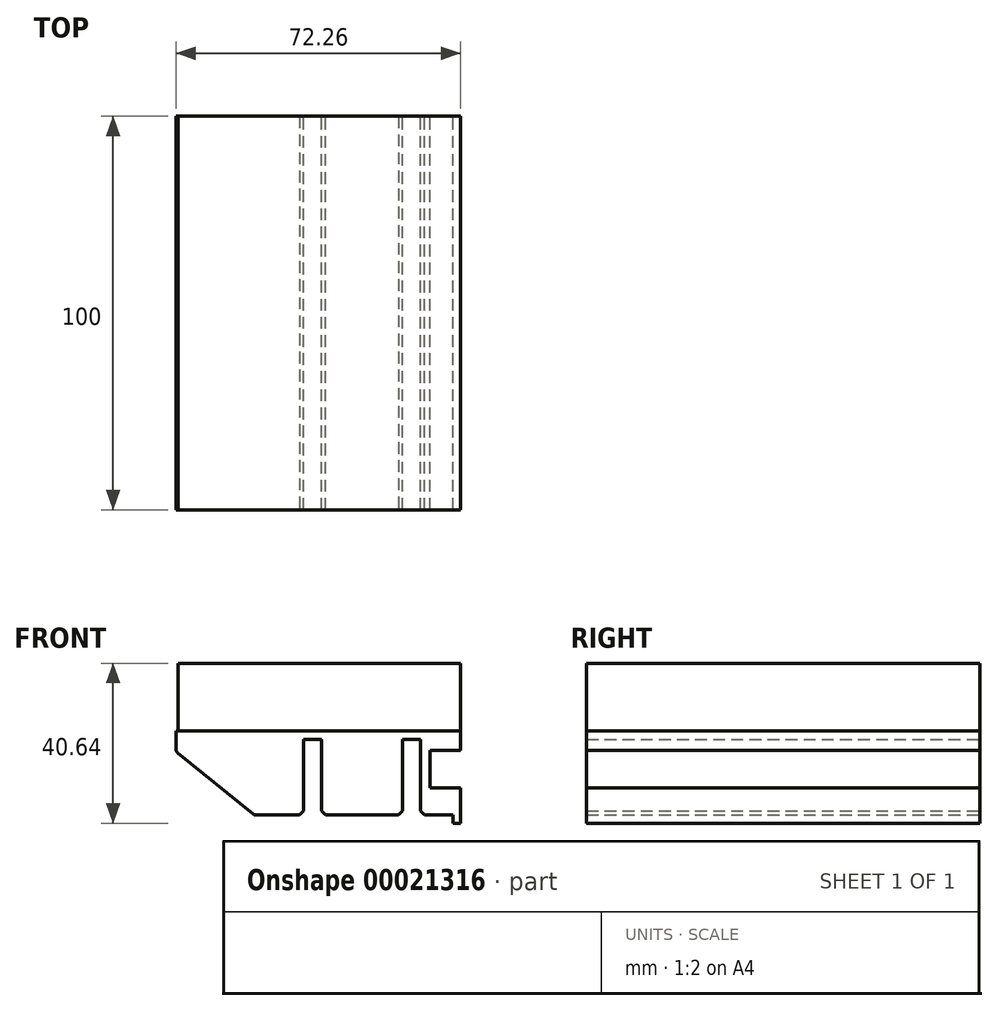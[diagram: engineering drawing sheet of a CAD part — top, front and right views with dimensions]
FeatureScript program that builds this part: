
annotation { "Feature Type Name" : "Feature", "Feature Type Description" : "" }
export const myFeature = defineFeature(function(context is Context, id is Id, definition is map)
    precondition{}
    {
        {
            var Q0;
            Q0=qCreatedBy(makeId("Front.planeOp"),FACE);
            var sketch = newSketch(context, id + "F0", { "sketchPlane" : qUnion([Q0])});
            skLineSegment(sketch, "E0.bottom", {"start": v(0, 0) * mm, "end": v(71.76, 0) * mm});
            skLineSegment(sketch, "E0.top", {"start": v(-0.5, -17.2) * mm, "end": v(0, -17.2) * mm});
            skLineSegment(sketch, "E0.left", {"start": v(0, 0) * mm, "end": v(0, -17.2) * mm});
            skLineSegment(sketch, "E0.right", {"start": v(71.76, 0) * mm, "end": v(71.76, -17.2) * mm});
            skLineSegment(sketch, "E1", {"start": v(-0.5, -22.4) * mm, "end": v(19.36, -38.54) * mm});
            skLineSegment(sketch, "E2", {"start": v(19.36, -38.54) * mm, "end": v(31.89, -38.54) * mm});
            skLineSegment(sketch, "E3", {"start": v(31.89, -38.54) * mm, "end": v(31.89, -19.3) * mm});
            skLineSegment(sketch, "E4", {"start": v(31.89, -19.3) * mm, "end": v(36.46, -19.3) * mm});
            skLineSegment(sketch, "E5", {"start": v(36.46, -19.3) * mm, "end": v(36.46, -38.54) * mm});
            skLineSegment(sketch, "E6", {"start": v(36.46, -38.54) * mm, "end": v(57, -38.54) * mm});
            skLineSegment(sketch, "E7", {"start": v(-0.5, -22.4) * mm, "end": v(-0.5, -17.2) * mm});
            skLineSegment(sketch, "E8", {"start": v(0, -17.2) * mm, "end": v(71.76, -17.2) * mm});
            skLineSegment(sketch, "E9.top", {"start": v(57, -19.3) * mm, "end": v(61.6, -19.3) * mm});
            skLineSegment(sketch, "E9.left", {"start": v(57, -38.54) * mm, "end": v(57, -19.3) * mm});
            skLineSegment(sketch, "E9.right", {"start": v(61.6, -38.54) * mm, "end": v(61.6, -19.3) * mm});
            skLineSegment(sketch, "E10.top", {"start": v(71.76, -40.64) * mm, "end": v(69.81, -40.64) * mm});
            skLineSegment(sketch, "E10.left", {"start": v(71.76, -31.64) * mm, "end": v(71.76, -40.64) * mm});
            skLineSegment(sketch, "E10.right", {"start": v(69.81, -38.54) * mm, "end": v(69.81, -40.64) * mm});
            skLineSegment(sketch, "E11.bottom", {"start": v(71.76, -31.64) * mm, "end": v(63.96, -31.64) * mm});
            skLineSegment(sketch, "E11.top", {"start": v(71.76, -22.14) * mm, "end": v(63.96, -22.14) * mm});
            skLineSegment(sketch, "E11.right", {"start": v(63.96, -31.64) * mm, "end": v(63.96, -22.14) * mm});
            skLineSegment(sketch, "E12", {"start": v(61.6, -38.54) * mm, "end": v(69.81, -38.54) * mm});
            skLineSegment(sketch, "E13", {"start": v(71.76, -22.14) * mm, "end": v(71.76, -17.2) * mm});
            skSolve(sketch);
        }
        {
            var Q0;
            Q0=makeQuery(id+"F0.imprint","IMPRINT",FACE,{"disambiguationData":[TD([[makeQuery(id+"F0.imprint","IMPRINT",EDGE,{"derivedFrom":sQuery(id+"F0.wireOp",EDGE,"E0.top")}),-1.0]])]});
            extrude(context, id + "F1", {"entities" : qUnion([Q0]), "endBound" : BoundingType.SYMMETRIC, "depth" : 100 * mm});
        }
        {
            var Q0;
            Q0=makeQuery(id+"F1.opExtrude","SWEPT_EDGE",EDGE,{"disambiguationData":[OSD([sQuery(id+"F0.wireOp",EDGE,"E2"),sQuery(id+"F0.wireOp",EDGE,"E3")])]});
            var Q1;
            Q1=makeQuery(id+"F1.opExtrude","SWEPT_EDGE",EDGE,{"disambiguationData":[OSD([sQuery(id+"F0.wireOp",EDGE,"E5"),sQuery(id+"F0.wireOp",EDGE,"E6")])]});
            var Q2;
            Q2=makeQuery(id+"F1.opExtrude","SWEPT_EDGE",EDGE,{"disambiguationData":[OSD([sQuery(id+"F0.wireOp",EDGE,"E6"),sQuery(id+"F0.wireOp",EDGE,"E9.left")])]});
            var Q3;
            Q3=makeQuery(id+"F1.opExtrude","SWEPT_EDGE",EDGE,{"disambiguationData":[OSD([sQuery(id+"F0.wireOp",EDGE,"E9.right"),sQuery(id+"F0.wireOp",EDGE,"E12")])]});
            chamfer(context, id + "F2", {"entities" : qUnion([Q0, Q1, Q2, Q3]), "width" : 1 * mm, "tangentPropagation" : true});
        }
        {
            var Q0;
            Q0=makeQuery(id+"F1.opExtrude","SWEPT_EDGE",EDGE,{"disambiguationData":[OSD([sQuery(id+"F0.wireOp",EDGE,"E1"),sQuery(id+"F0.wireOp",EDGE,"E2")])]});
            var Q1;
            Q1=makeQuery(id+"F1.opExtrude","SWEPT_EDGE",EDGE,{"disambiguationData":[OSD([sQuery(id+"F0.wireOp",EDGE,"E1"),sQuery(id+"F0.wireOp",EDGE,"E7")])]});
            fillet(context, id + "F3", {"entities" : qUnion([Q0, Q1]), "radius" : 1 * mm, "tangentPropagation" : true, "allowEdgeOverflow" : false});
        }
        {
            var Q0;
            Q0=makeQuery(id+"F0.imprint","IMPRINT",FACE,{"disambiguationData":[TD([[makeQuery(id+"F0.imprint","IMPRINT",EDGE,{"derivedFrom":sQuery(id+"F0.wireOp",EDGE,"E0.bottom")}),-1.0]])]});
            extrude(context, id + "F4", {"entities" : qUnion([Q0]), "endBound" : BoundingType.SYMMETRIC, "depth" : 100 * mm});
        }
    });
